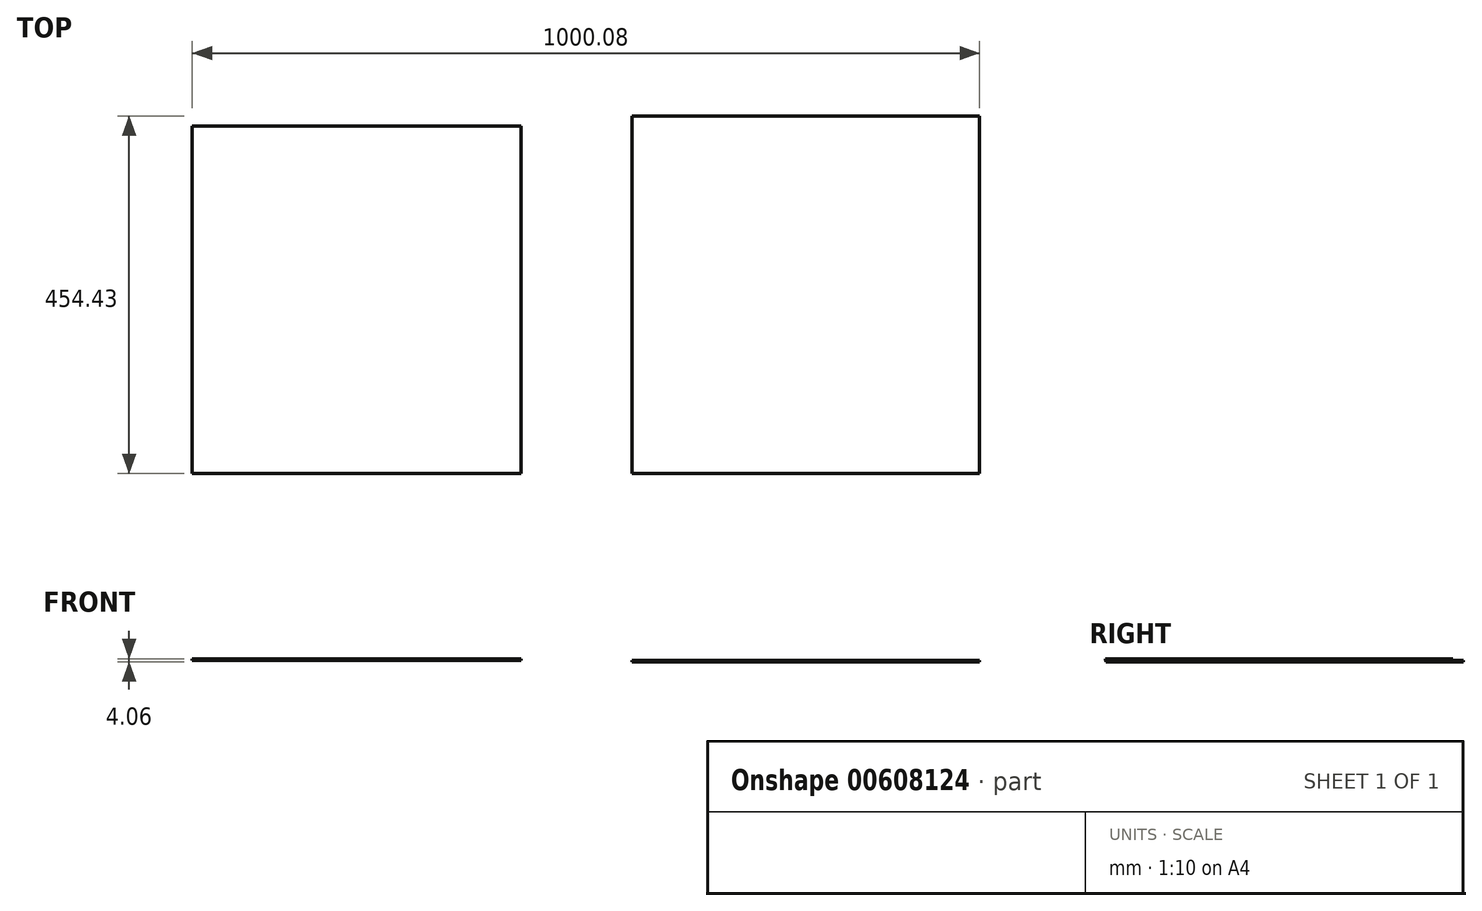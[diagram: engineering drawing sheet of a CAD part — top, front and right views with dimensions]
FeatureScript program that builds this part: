
annotation { "Feature Type Name" : "Feature", "Feature Type Description" : "" }
export const myFeature = defineFeature(function(context is Context, id is Id, definition is map)
    precondition{}
    {
        {
            var Q0;
            Q0=qCreatedBy(makeId("Top.planeOp"),FACE);
            var sketch = newSketch(context, id + "F0", { "sketchPlane" : qUnion([Q0])});
            skLineSegment(sketch, "E0.bottom", {"start": v(220.66, -227.01) * mm, "end": v(-220.66, -227.01) * mm});
            skLineSegment(sketch, "E0.top", {"start": v(220.66, 227.01) * mm, "end": v(-220.66, 227.01) * mm});
            skLineSegment(sketch, "E0.left", {"start": v(220.66, -227.01) * mm, "end": v(220.66, 227.01) * mm});
            skLineSegment(sketch, "E0.right", {"start": v(-220.66, -227.01) * mm, "end": v(-220.66, 227.01) * mm});
            skPoint(sketch, "E0.middle", {"position": v(0, 0) * mm});
            skLineSegment(sketch, "E1.bottom", {"start": v(-220.66, -227.01) * mm, "end": v(-217.49, -227.01) * mm});
            skLineSegment(sketch, "E1.left", {"start": v(-220.66, -227.01) * mm, "end": v(-220.66, -144.46) * mm});
            skLineSegment(sketch, "E2.bottom", {"start": v(220.66, -227.01) * mm, "end": v(217.49, -227.01) * mm});
            skLineSegment(sketch, "E2.left", {"start": v(220.66, -227.01) * mm, "end": v(220.66, -144.46) * mm});
            skSolve(sketch);
        }
        {
            var Q0;
            Q0=makeQuery(id+"F0.imprint","IMPRINT",FACE,{"disambiguationData":[TD([[makeQuery(id+"F0.imprint","IMPRINT",EDGE,{"derivedFrom":sQuery(id+"F0.wireOp",EDGE,"E0.bottom")}),-1.0]])]});
            extrude(context, id + "F1", {"entities" : qUnion([Q0]), "depth" : 2.03 * mm, "offsetDistance" : 25.4 * mm});
        }
        {
            var Q0;
            Q0=makeQuery(id+"F1.opExtrude","CAP_FACE",FACE,{"disambiguationData":[OSD([sQuery(id+"F0.wireOp",EDGE,"E0.bottom"),sQuery(id+"F0.wireOp",EDGE,"E0.top"),sQuery(id+"F0.wireOp",EDGE,"E0.left"),sQuery(id+"F0.wireOp",EDGE,"E0.right"),sQuery(id+"F0.wireOp",EDGE,"E1.bottom"),sQuery(id+"F0.wireOp",EDGE,"E1.left"),sQuery(id+"F0.wireOp",EDGE,"E2.bottom"),sQuery(id+"F0.wireOp",EDGE,"E2.left")])],"isStart":false});
            var sketch = newSketch(context, id + "F2", { "sketchPlane" : qUnion([Q0])});
            skLineSegment(sketch, "E3.bottom", {"start": v(-361.9, -227.42) * mm, "end": v(-779.42, -227.42) * mm});
            skLineSegment(sketch, "E3.top", {"start": v(-361.9, 213.9) * mm, "end": v(-779.42, 213.9) * mm});
            skLineSegment(sketch, "E3.left", {"start": v(-361.9, -227.42) * mm, "end": v(-361.9, 213.9) * mm});
            skLineSegment(sketch, "E3.right", {"start": v(-779.42, -227.42) * mm, "end": v(-779.42, 213.9) * mm});
            skSolve(sketch);
        }
        {
            var Q0;
            Q0=makeQuery(id+"F2.imprint","IMPRINT",FACE,{"disambiguationData":[TD([[makeQuery(id+"F2.imprint","IMPRINT",EDGE,{"derivedFrom":sQuery(id+"F2.wireOp",EDGE,"1BgGyHGM-FOAu-MDjo-izlG-MtHqZyXujZSA.bottom")}),1.0]])]});
            var Q1;
            Q1=makeQuery(id+"F2.imprint","IMPRINT",FACE,{"disambiguationData":[TD([[makeQuery(id+"F2.imprint","IMPRINT",EDGE,{"derivedFrom":sQuery(id+"F2.wireOp",EDGE,"E3.bottom")}),-1.0]])]});
            extrude(context, id + "F3", {"entities" : qUnion([Q0, Q1]), "depth" : 2.03 * mm, "offsetDistance" : 25.4 * mm});
        }
    });
